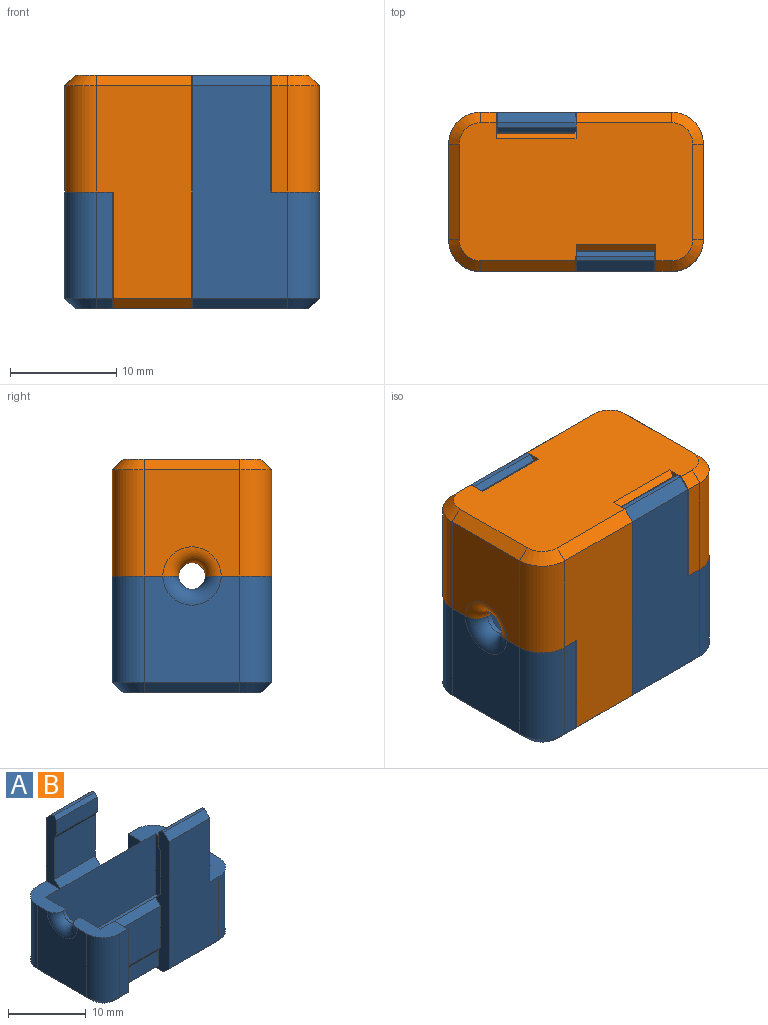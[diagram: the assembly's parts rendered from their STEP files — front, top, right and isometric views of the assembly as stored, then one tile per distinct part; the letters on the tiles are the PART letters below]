
ASSEMBLY  parts=2 mates=1
PART A: 64 faces, bbox 24x15x22 mm
  f0: plane 6.25x4.6mm, normal (0,0,1), area 16.6mm2, adj f8,f9,f12,f13,f17,f35,f44,f58
  f1: plane 20x9mm, normal (0,1,0), area 164mm2, adj f3,f23,f41,f42,f55,f56
  f2: plane 10x1.5mm, normal (0,-1,0), area 15mm2, adj f5,f28,f43,f51
  f3: plane 6.25x4.6mm, normal (0,0,1), area 16.6mm2, adj f1,f7,f10,f11,f16,f41,f42,f59
  f4: plane 22x13mm, normal (0,0,-1), area 260.1mm2, adj f22,f23,f28,f29,f46,f47,f48,f49
  f5: plane 6.25x4.5mm, normal (0,0,1), area 16.3mm2, adj f2,f7,f10,f13,f16,f28,f43,f59
  f6: plane 10x1.5mm, normal (0,1,0), area 15mm2, adj f14,f22,f45,f50
  f7: plane 10x9mm, normal (-1,0,0), area 78.1mm2, adj f3,f5,f42,f43,f53,f59
  f8: plane 20x9mm, normal (0,-1,0), area 164mm2, adj f0,f29,f35,f44,f46,f57
  f9: plane 10x9mm, normal (1,0,0), area 78.1mm2, adj f0,f14,f44,f45,f48,f58
  f10: plane 10x9.5mm, normal (1,0,0), area 92.5mm2, adj f3,f5,f11,f13,f15,f16
  f11: plane 20x9.5mm, normal (0,-1,0), area 190mm2, adj f3,f10,f12,f14,f15,f18,f40
  f12: plane 10x9.5mm, normal (-1,0,0), area 92.5mm2, adj f0,f11,f13,f14,f15,f17
  f13: plane 20x9.5mm, normal (0,1,0), area 190mm2, adj f0,f5,f10,f12,f15,f24,f34
  f14: plane 6.25x4.5mm, normal (0,0,1), area 16.3mm2, adj f6,f9,f11,f12,f17,f22,f45,f58
  f15: plane 20x10mm, normal (0,0,1), area 200mm2, adj f10,f11,f12,f13
  f16: cylinder r=1.25mm len=2.5mm, axis (1,0,0), area 2mm2, adj f3,f5,f10,f59
  f17: cylinder r=1.25mm len=2.5mm, axis (1,0,0), area 2mm2, adj f0,f12,f14,f58
  f18: plane 7.5x0.9mm, normal (0,0.71,0.71), area 9.5mm2, adj f11,f19,f22,f23
  f19: plane 7.5x6.51mm, normal (0,1,0), area 48.8mm2, adj f18,f20,f22,f23
  f20: plane 7.5x0.69mm, normal (0,0.87,-0.5), area 6mm2, adj f19,f21,f22,f23
  f21: plane 7.5x2.4mm, normal (0,1,0), area 18mm2, adj f20,f22,f23,f62
  f22: plane 11x2.5mm, normal (-1,0,0), area 18.9mm2, adj f4,f6,f14,f18,f19,f20,f21,f50
  f23: plane 22x2.5mm, normal (1,0,0), area 36.6mm2, adj f1,f4,f18,f19,f20,f21,f36,f37
  f24: plane 7.5x0.9mm, normal (0,-0.71,0.71), area 9.5mm2, adj f13,f25,f28,f29
  f25: plane 7.5x6.51mm, normal (0,-1,0), area 48.8mm2, adj f24,f26,f28,f29
  f26: plane 7.5x0.69mm, normal (0,-0.87,-0.5), area 6mm2, adj f25,f27,f28,f29
  f27: plane 7.5x2.4mm, normal (0,-1,0), area 18mm2, adj f26,f28,f29,f63
  f28: plane 11x2.5mm, normal (1,0,0), area 18.9mm2, adj f2,f4,f5,f24,f25,f26,f27,f51
  f29: plane 22x2.5mm, normal (-1,0,0), area 36.6mm2, adj f4,f8,f24,f25,f26,f27,f30,f31
  f30: plane 7.4x6.51mm, normal (0,1,0), area 48.2mm2, adj f29,f31,f34,f35
  f31: plane 7.4x0.69mm, normal (0,0.87,-0.5), area 5.9mm2, adj f29,f30,f32,f35
  f32: plane 7.4x2.3mm, normal (0,1,0), area 17mm2, adj f29,f31,f35,f61
  f33: plane 7.4x0.4mm, normal (0,0,1), area 3mm2, adj f29,f35,f57,f61
  f34: plane 7.4x1mm, normal (0,0.71,0.71), area 10.5mm2, adj f13,f29,f30,f35
  f35: plane 11x2.5mm, normal (1,0,0), area 17.6mm2, adj f0,f8,f30,f31,f32,f33,f34,f57
  f36: plane 7.4x6.51mm, normal (0,-1,0), area 48.2mm2, adj f23,f37,f40,f41
  f37: plane 7.4x0.69mm, normal (0,-0.87,-0.5), area 5.9mm2, adj f23,f36,f38,f41
  f38: plane 7.4x2.3mm, normal (0,-1,0), area 17mm2, adj f23,f37,f41,f60
  f39: plane 7.4x0.4mm, normal (0,0,1), area 3mm2, adj f23,f41,f56,f60
  f40: plane 7.4x1mm, normal (0,-0.71,0.71), area 10.5mm2, adj f11,f23,f36,f41
  f41: plane 11x2.5mm, normal (-1,0,0), area 17.6mm2, adj f1,f3,f36,f37,f38,f39,f40,f56
  f42: cylinder r=3mm len=10mm, axis (0,0,-1), area 47.1mm2, adj f1,f3,f7,f54
  f43: cylinder r=3mm len=10mm, axis (0,0,1), area 47.1mm2, adj f2,f5,f7,f52
  f44: cylinder r=3mm len=10mm, axis (0,0,-1), area 47.1mm2, adj f0,f8,f9,f47
  f45: cylinder r=3mm len=10mm, axis (0,0,1), area 47.1mm2, adj f6,f9,f14,f49
  f46: plane 9x1mm, normal (0,-0.71,-0.71), area 12.7mm2, adj f4,f8,f29,f47
  f47: cone r=2mm half-angle=45deg, axis (0,0,1), area 5.6mm2, adj f4,f44,f46,f48
  f48: plane 9x1mm, normal (0.71,0,-0.71), area 12.7mm2, adj f4,f9,f47,f49
  f49: cone r=2mm half-angle=45deg, axis (0,0,1), area 5.6mm2, adj f4,f45,f48,f50
  f50: plane 1.5x1mm, normal (0,0.71,-0.71), area 2.1mm2, adj f4,f6,f22,f49
  f51: plane 1.5x1mm, normal (0,-0.71,-0.71), area 2.1mm2, adj f2,f4,f28,f52
  f52: cone r=2mm half-angle=45deg, axis (0,0,1), area 5.6mm2, adj f4,f43,f51,f53
  f53: plane 9x1mm, normal (-0.71,0,-0.71), area 12.7mm2, adj f4,f7,f52,f54
  f54: cone r=2mm half-angle=45deg, axis (0,0,1), area 5.6mm2, adj f4,f42,f53,f55
  f55: plane 9x1mm, normal (0,0.71,-0.71), area 12.7mm2, adj f1,f4,f23,f54
  f56: plane 7.4x1mm, normal (0,0.71,0.71), area 10.5mm2, adj f1,f23,f39,f41
  f57: plane 7.4x1mm, normal (0,-0.71,0.71), area 10.5mm2, adj f8,f29,f33,f35
  f58: torus R=2.75mm, axis (-1,0,0), area 13.3mm2, adj f0,f9,f14,f17
  f59: torus R=2.75mm, axis (-1,0,0), area 13.3mm2, adj f3,f5,f7,f16
  f60: plane 7.4x0.5mm, normal (0,-0.71,0.71), area 5.2mm2, adj f23,f38,f39,f41
  f61: plane 7.4x0.5mm, normal (0,0.71,0.71), area 5.2mm2, adj f29,f32,f33,f35
  f62: plane 7.5x0.5mm, normal (0,0.71,-0.71), area 5.3mm2, adj f4,f21,f22,f23
  f63: plane 7.5x0.5mm, normal (0,-0.71,-0.71), area 5.3mm2, adj f4,f27,f28,f29
PART B: same geometry as A
PLACE A at identity fixed
PLACE B rot(axis=(1,0,0),180deg) t=(0,0,19)mm
MATE fastened A.f3 <-> B.f5  axis (0,0,1) through (-10,5,9.5)mm
